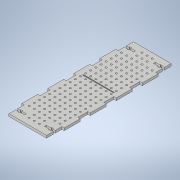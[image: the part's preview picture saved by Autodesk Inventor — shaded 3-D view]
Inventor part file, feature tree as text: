
AUTODESK INVENTOR PART (.ipt)
format: ipt  version: 2022.1 (Build 261234020, 234B)  size: 452,608 bytes
history: native  units: in
note: dims shown in document units (in); Inventor stores cm internally (conversion verified against a paired STEP export)
features: sketch x7, extrude x6, hole x3, pattern_linear x3, other x3, reference x2, projected_geometry x1
ambient origin geometry x8: Origin, YZ Plane, XZ Plane, XY Plane, X Axis, Y Axis, Z Axis, Center Point
bodies: Solid1 (feature_tree)
feature tree (25):
  extrude  "Base"  Depth=12.1518in
  hole  "Board Hole"  [1 undecoded]
  pattern_linear  "Patterned Board Holes"  Count1=19 Spacing1=0.5in
  extrude  "Extrusion4"  Depth=1.0in TaperAngle=0.0deg
  hole  "Hole9"  [1 undecoded]
  extrude  "Extrusion6"  Depth=1.4976in
  extrude  "Extrusion7"  Depth=0.2313in
  extrude  "Extrusion8"  Depth=0.2313in
  pattern_linear  "Rectangular Pattern6"  Spacing1=1.4976in  [1 undecoded]
  sketch  "Sketch19"  dims[d132=0.1673in d133=0.75in d134=0.375in d135=0.25in d136=0.5635in d137=1.0in d138=0.8108in d154=1.0in d155=0.0in]
  extrude  "Extrusion10"  Depth=0.3348in TaperAngle=0.0deg
  hole  "Hole10"  [1 undecoded]
  pattern_linear  "Rectangular Pattern8"  Spacing1=1.4976in  [1 undecoded]
  sketch  "Sketch1"  dims[d0=4.1323in d1=12.1518in]
  sketch  "Sketch7"  dims[d2=0.2362in d3=0.0in d35=1.5in]
  projected_geometry  "Projected Loop1"
  sketch  "Sketch12"  dims[d36=2.0661in]
  sketch  "Sketch16"  dims[d37=0.1673in d38=0.315in d39=0.175in d40=0.25in d41=0.5635in d42=0.465in d43=0.8108in d44=7.4803in d46=0.5in]
  sketch  "Sketch18"  dims[d47=2.7559in d49=0.5in d97=1.0in d98=0.0in]
  sketch  "Sketch20"  dims[d163=0.5in d175=1.4976in d176=0.2313in d178=0.2313in d179=1.4976in d180=1.0in d181=0.0in d188=0.2313in d189=1.4976in d190=0.2313in d191=1.4976in d217=1.0in d218=0.0in d219=0.7874in d221=0.5in d222=1.1811in d224=0.5in d225=0.128in d234=0.1in d235=0.0394in d236=0.0in d237=1.1073in d238=0.1673in d239=0.3248in d240=0.4724in d242=0.6664in d243=0.1673in d244=0.2362in d245=0.3701in d246=0.0787in d247=90.0deg d248=0.315in d249=0.8108in d250=1.1811in d252=0.5in d253=0.7874in d255=0.5in d256=0.177in d257=0.2313in d258=0.9854in d259=0.2313in d260=0.9854in d261=0.2313in d262=0.9854in d264=3.5404in d266=3.5404in d269=6.0759in d270=2.0661in d271=3.0in d272=0.3348in d273=0.2in]
  reference  "Reference1"
  reference  "Reference2"
  other  "<userpath>\Desktop\P3 Bracket Files\V4 Baseplate no QBot.iam"
  other  "V4 Baseplate no QBot.iam"
  other  "V3 Mounting Wall:1"
note: 5 required parameter values undecoded (feature->parameter linkage not recoverable at this tier; creation-order binding heuristic only, values carry confidence <= 0.55)
